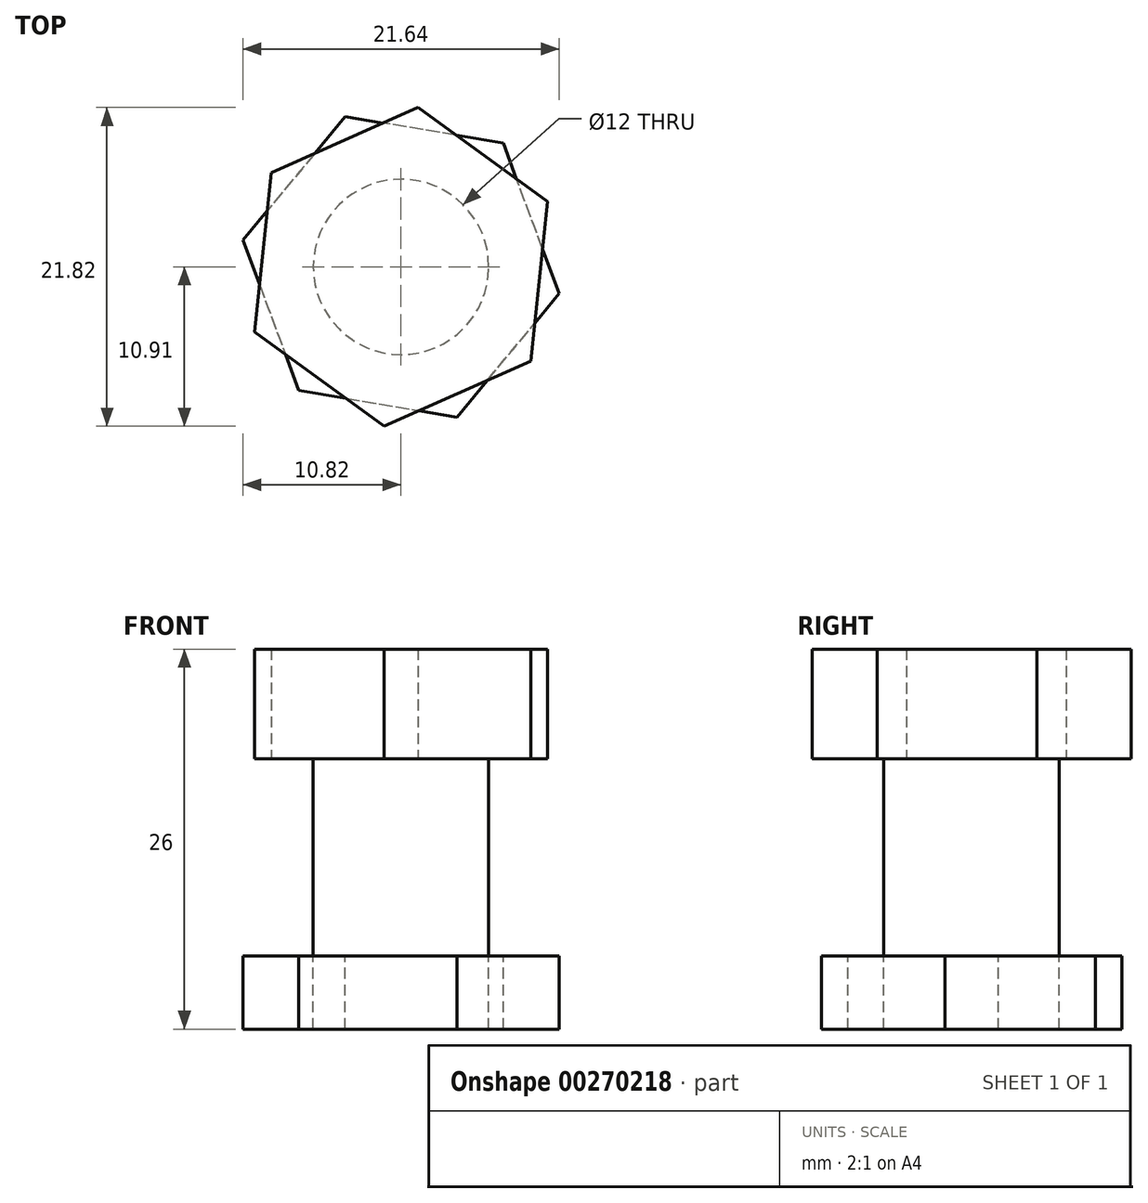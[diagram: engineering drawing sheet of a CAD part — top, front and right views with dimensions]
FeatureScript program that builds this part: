
annotation { "Feature Type Name" : "Feature", "Feature Type Description" : "" }
export const myFeature = defineFeature(function(context is Context, id is Id, definition is map)
    precondition{}
    {
        {
            var Q0;
            Q0=qCreatedBy(makeId("Top.planeOp"),FACE);
            var sketch = newSketch(context, id + "F0", { "sketchPlane" : qUnion([Q0])});
            skCircle(sketch, "E0.cCircle", {"center": v(0, 0) * mm, "radius": 9.5 * mm, "construction": true});
            skLineSegment(sketch, "E0.0", {"start": v(-10.02, -4.46) * mm, "end": v(-8.87, 6.45) * mm});
            skLineSegment(sketch, "E0.1", {"start": v(-8.87, 6.45) * mm, "end": v(1.15, 10.9) * mm});
            skLineSegment(sketch, "E0.2", {"start": v(1.15, 10.9) * mm, "end": v(10.02, 4.46) * mm});
            skLineSegment(sketch, "E0.3", {"start": v(10.02, 4.46) * mm, "end": v(8.87, -6.45) * mm});
            skLineSegment(sketch, "E0.4", {"start": v(8.87, -6.45) * mm, "end": v(-1.15, -10.9) * mm});
            skLineSegment(sketch, "E0.5", {"start": v(-1.15, -10.9) * mm, "end": v(-10.02, -4.46) * mm});
            skPoint(sketch, "E0.0.midPoint", {"position": v(-9.45, 1) * mm});
            skSolve(sketch);
        }
        {
            var Q0;
            Q0=makeQuery(id+"F0.imprint","IMPRINT",FACE,{"disambiguationData":[TD([[makeQuery(id+"F0.imprint","IMPRINT",EDGE,{"derivedFrom":sQuery(id+"F0.wireOp",EDGE,"E0.0")}),-1.0]])]});
            extrude(context, id + "F1", {"entities" : qUnion([Q0]), "depth" : 7.5 * mm});
        }
        {
            var Q0;
            Q0=makeQuery(id+"F1.opExtrude","CAP_FACE",FACE,{"disambiguationData":[OSD([sQuery(id+"F0.wireOp",EDGE,"E0.0"),sQuery(id+"F0.wireOp",EDGE,"E0.1"),sQuery(id+"F0.wireOp",EDGE,"E0.2"),sQuery(id+"F0.wireOp",EDGE,"E0.3"),sQuery(id+"F0.wireOp",EDGE,"E0.4"),sQuery(id+"F0.wireOp",EDGE,"E0.5")])],"isStart":true});
            var sketch = newSketch(context, id + "F2", { "sketchPlane" : qUnion([Q0])});
            skCircle(sketch, "E1", {"center": v(0, 0) * mm, "radius": 6 * mm});
            skSolve(sketch);
        }
        {
            var Q0;
            Q0=makeQuery(id+"F2.imprint","IMPRINT",FACE,{"disambiguationData":[TD([[makeQuery(id+"F2.imprint","IMPRINT",EDGE,{"derivedFrom":sQuery(id+"F2.wireOp",EDGE,"E1")}),1.0]])]});
            extrude(context, id + "F3", {"entities" : qUnion([Q0]), "operationType" : NewBodyOperationType.ADD, "depth" : 13.5 * mm});
        }
        {
            var Q0;
            Q0=makeQuery(id+"F3.opExtrude","CAP_FACE",FACE,{"disambiguationData":[OSD([sQuery(id+"F2.wireOp",EDGE,"E1")])],"isStart":false});
            var sketch = newSketch(context, id + "F4", { "sketchPlane" : qUnion([Q0])});
            skCircle(sketch, "E2.cCircle", {"center": v(0, 0) * mm, "radius": 9.5 * mm, "construction": true});
            skLineSegment(sketch, "E2.0", {"start": v(10.82, 1.82) * mm, "end": v(6.99, -8.46) * mm});
            skLineSegment(sketch, "E2.1", {"start": v(6.99, -8.46) * mm, "end": v(-3.83, -10.28) * mm});
            skLineSegment(sketch, "E2.2", {"start": v(-3.83, -10.28) * mm, "end": v(-10.82, -1.82) * mm});
            skLineSegment(sketch, "E2.3", {"start": v(-10.82, -1.82) * mm, "end": v(-6.99, 8.46) * mm});
            skLineSegment(sketch, "E2.4", {"start": v(-6.99, 8.46) * mm, "end": v(3.83, 10.28) * mm});
            skLineSegment(sketch, "E2.5", {"start": v(3.83, 10.28) * mm, "end": v(10.82, 1.82) * mm});
            skPoint(sketch, "E2.0.midPoint", {"position": v(8.9, -3.32) * mm});
            skCircle(sketch, "E3", {"center": v(0, 0) * mm, "radius": 6 * mm});
            skSolve(sketch);
        }
        {
            var Q0;
            Q0 = qSketchRegion(id + "F4", true);
            extrude(context, id + "F5", {"entities" : qUnion([Q0]), "depth" : 5 * mm});
        }
    });
